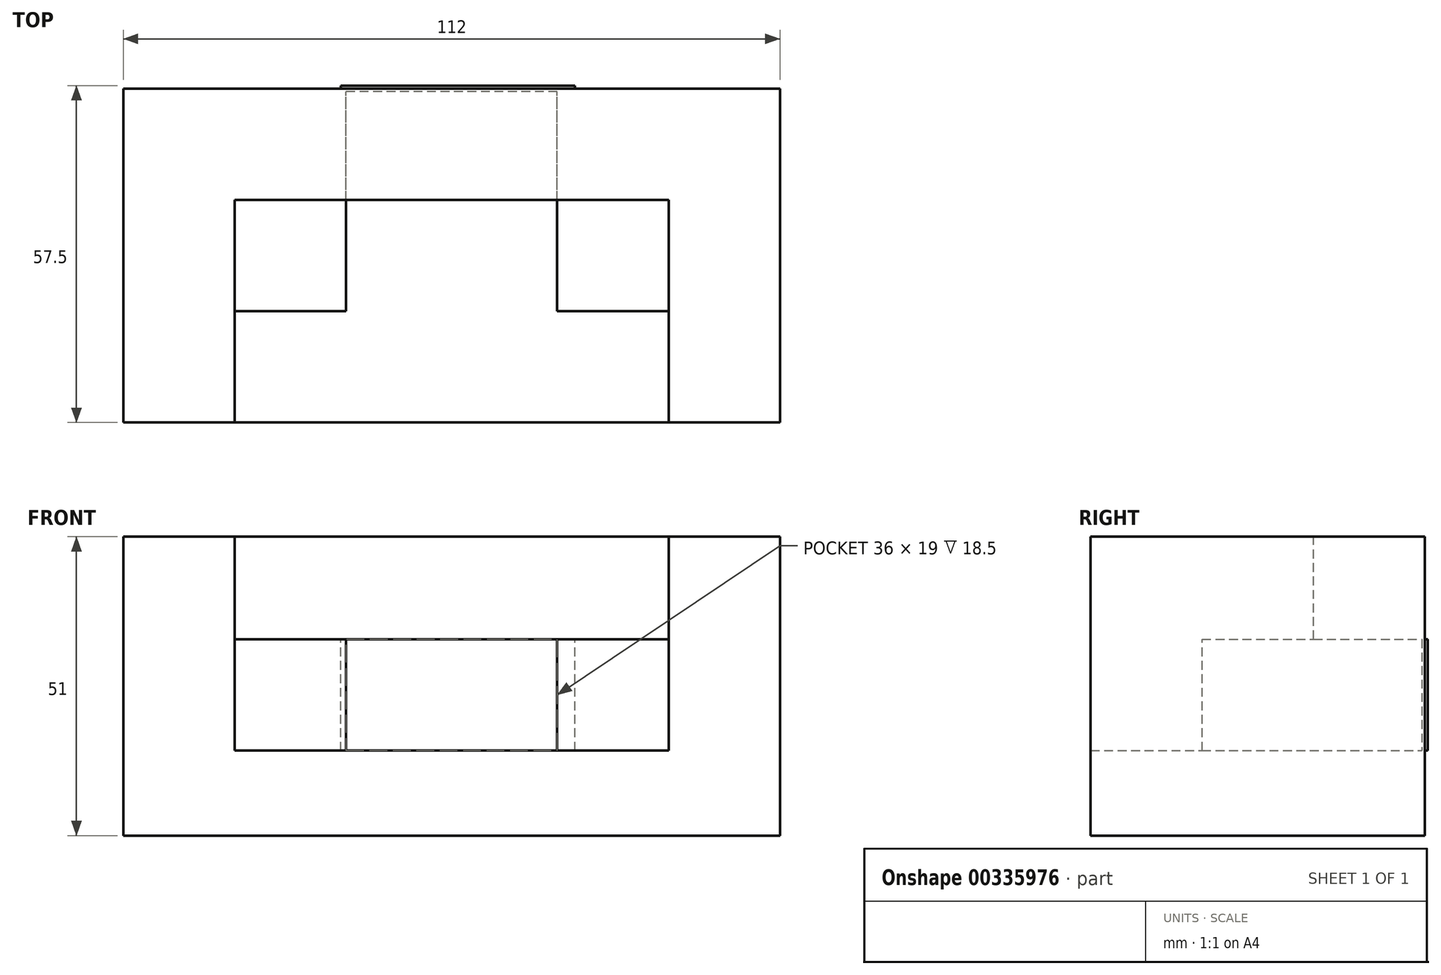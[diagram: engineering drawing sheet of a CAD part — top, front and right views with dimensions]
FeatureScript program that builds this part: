
annotation { "Feature Type Name" : "Feature", "Feature Type Description" : "" }
export const myFeature = defineFeature(function(context is Context, id is Id, definition is map)
    precondition{}
    {
        {
            var Q0;
            Q0=qCreatedBy(makeId("Front.planeOp"),FACE);
            var sketch = newSketch(context, id + "F0", { "sketchPlane" : qUnion([Q0])});
            skLineSegment(sketch, "E0", {"start": v(0, 0) * mm, "end": v(56, 0) * mm});
            skLineSegment(sketch, "E1", {"start": v(56, 0) * mm, "end": v(56, 51) * mm});
            skLineSegment(sketch, "E2", {"start": v(56, 51) * mm, "end": v(37, 51) * mm});
            skLineSegment(sketch, "E3", {"start": v(0, 0) * mm, "end": v(-56, 0) * mm});
            skLineSegment(sketch, "E4", {"start": v(-56, 0) * mm, "end": v(-56, 51) * mm});
            skLineSegment(sketch, "E5", {"start": v(-56, 51) * mm, "end": v(-37, 51) * mm});
            skLineSegment(sketch, "E6", {"start": v(-37, 51) * mm, "end": v(-37, 14.5) * mm});
            skLineSegment(sketch, "E7", {"start": v(-37, 14.5) * mm, "end": v(37, 14.5) * mm});
            skLineSegment(sketch, "E8", {"start": v(37, 14.5) * mm, "end": v(37, 51) * mm});
            skSolve(sketch);
        }
        {
            var Q0;
            Q0 = qSketchRegion(id + "F0", true);
            extrude(context, id + "F1", {"entities" : qUnion([Q0]), "depth" : 57 * mm});
        }
        {
            var Q0;
            Q0=makeQuery(id+"F1.opExtrude","CAP_FACE",FACE,{"disambiguationData":[OSD([sQuery(id+"F0.wireOp",EDGE,"E0"),sQuery(id+"F0.wireOp",EDGE,"E1"),sQuery(id+"F0.wireOp",EDGE,"E2"),sQuery(id+"F0.wireOp",EDGE,"E3"),sQuery(id+"F0.wireOp",EDGE,"E4"),sQuery(id+"F0.wireOp",EDGE,"E5"),sQuery(id+"F0.wireOp",EDGE,"E6"),sQuery(id+"F0.wireOp",EDGE,"E7"),sQuery(id+"F0.wireOp",EDGE,"E8")])],"isStart":true});
            var sketch = newSketch(context, id + "F2", { "sketchPlane" : qUnion([Q0])});
            skLineSegment(sketch, "E9.bottom", {"start": v(37, 14.5) * mm, "end": v(18, 14.5) * mm});
            skLineSegment(sketch, "E9.top", {"start": v(37, 33.5) * mm, "end": v(18, 33.5) * mm});
            skLineSegment(sketch, "E9.left", {"start": v(37, 14.5) * mm, "end": v(37, 33.5) * mm});
            skLineSegment(sketch, "E9.right", {"start": v(18, 14.5) * mm, "end": v(18, 33.5) * mm});
            skLineSegment(sketch, "E10.bottom", {"start": v(-37, 14.5) * mm, "end": v(-18, 14.5) * mm});
            skLineSegment(sketch, "E10.top", {"start": v(-37, 33.5) * mm, "end": v(-18, 33.5) * mm});
            skLineSegment(sketch, "E10.left", {"start": v(-37, 14.5) * mm, "end": v(-37, 33.5) * mm});
            skLineSegment(sketch, "E10.right", {"start": v(-18, 14.5) * mm, "end": v(-18, 33.5) * mm});
            skSolve(sketch);
        }
        {
            var Q0;
            Q0 = qSketchRegion(id + "F2", true);
            extrude(context, id + "F3", {"entities" : qUnion([Q0]), "operationType" : NewBodyOperationType.ADD, "oppositeDirection" : true, "depth" : 38 * mm});
        }
        {
            var Q0;
            Q0=makeQuery(id+"F3.boolean.opBoolean","MERGE",FACE,{"derivedFrom":[makeQuery(id+"F1.opExtrude","CAP_FACE",FACE,{"disambiguationData":[OSD([sQuery(id+"F0.wireOp",EDGE,"E0"),sQuery(id+"F0.wireOp",EDGE,"E1"),sQuery(id+"F0.wireOp",EDGE,"E2"),sQuery(id+"F0.wireOp",EDGE,"E3"),sQuery(id+"F0.wireOp",EDGE,"E4"),sQuery(id+"F0.wireOp",EDGE,"E5"),sQuery(id+"F0.wireOp",EDGE,"E6"),sQuery(id+"F0.wireOp",EDGE,"E7"),sQuery(id+"F0.wireOp",EDGE,"E8")])],"isStart":true}),makeQuery(id+"F3.opExtrude","CAP_FACE",FACE,{"disambiguationData":[OSD([sQuery(id+"F2.wireOp",EDGE,"E9.bottom"),sQuery(id+"F2.wireOp",EDGE,"E9.top"),sQuery(id+"F2.wireOp",EDGE,"E9.left"),sQuery(id+"F2.wireOp",EDGE,"E9.right")])],"isStart":true}),makeQuery(id+"F3.opExtrude","CAP_FACE",FACE,{"disambiguationData":[OSD([sQuery(id+"F2.wireOp",EDGE,"E10.bottom"),sQuery(id+"F2.wireOp",EDGE,"E10.top"),sQuery(id+"F2.wireOp",EDGE,"E10.left"),sQuery(id+"F2.wireOp",EDGE,"E10.right")])],"isStart":true})]});
            var sketch = newSketch(context, id + "F4", { "sketchPlane" : qUnion([Q0])});
            skLineSegment(sketch, "E11.bottom", {"start": v(-37, 33.5) * mm, "end": v(37, 33.5) * mm});
            skLineSegment(sketch, "E11.top", {"start": v(-37, 51) * mm, "end": v(37, 51) * mm});
            skLineSegment(sketch, "E11.left", {"start": v(-37, 33.5) * mm, "end": v(-37, 51) * mm});
            skLineSegment(sketch, "E11.right", {"start": v(37, 33.5) * mm, "end": v(37, 51) * mm});
            skSolve(sketch);
        }
        {
            var Q0;
            Q0 = qSketchRegion(id + "F4", true);
            extrude(context, id + "F5", {"entities" : qUnion([Q0]), "operationType" : NewBodyOperationType.ADD, "oppositeDirection" : true, "depth" : 19 * mm});
        }
        {
            var Q0;
            Q0=makeQuery(id+"F5.boolean.opBoolean","MERGE",FACE,{"derivedFrom":[makeQuery(id+"F3.boolean.opBoolean","MERGE",FACE,{"derivedFrom":[makeQuery(id+"F1.opExtrude","CAP_FACE",FACE,{"disambiguationData":[OSD([sQuery(id+"F0.wireOp",EDGE,"E0"),sQuery(id+"F0.wireOp",EDGE,"E1"),sQuery(id+"F0.wireOp",EDGE,"E2"),sQuery(id+"F0.wireOp",EDGE,"E3"),sQuery(id+"F0.wireOp",EDGE,"E4"),sQuery(id+"F0.wireOp",EDGE,"E5"),sQuery(id+"F0.wireOp",EDGE,"E6"),sQuery(id+"F0.wireOp",EDGE,"E7"),sQuery(id+"F0.wireOp",EDGE,"E8")])],"isStart":true}),makeQuery(id+"F3.opExtrude","CAP_FACE",FACE,{"disambiguationData":[OSD([sQuery(id+"F2.wireOp",EDGE,"E9.bottom"),sQuery(id+"F2.wireOp",EDGE,"E9.top"),sQuery(id+"F2.wireOp",EDGE,"E9.left"),sQuery(id+"F2.wireOp",EDGE,"E9.right")])],"isStart":true}),makeQuery(id+"F3.opExtrude","CAP_FACE",FACE,{"disambiguationData":[OSD([sQuery(id+"F2.wireOp",EDGE,"E10.bottom"),sQuery(id+"F2.wireOp",EDGE,"E10.top"),sQuery(id+"F2.wireOp",EDGE,"E10.left"),sQuery(id+"F2.wireOp",EDGE,"E10.right")])],"isStart":true})]}),makeQuery(id+"F5.opExtrude","CAP_FACE",FACE,{"disambiguationData":[OSD([sQuery(id+"F4.wireOp",EDGE,"E11.bottom"),sQuery(id+"F4.wireOp",EDGE,"E11.top"),sQuery(id+"F4.wireOp",EDGE,"E11.left"),sQuery(id+"F4.wireOp",EDGE,"E11.right")])],"isStart":true})]});
            var sketch = newSketch(context, id + "F6", { "sketchPlane" : qUnion([Q0])});
            skLineSegment(sketch, "E12.bottom", {"start": v(-21.05, 33.5) * mm, "end": v(18.95, 33.5) * mm});
            skLineSegment(sketch, "E12.top", {"start": v(-21.05, 14.5) * mm, "end": v(18.95, 14.5) * mm});
            skLineSegment(sketch, "E12.left", {"start": v(-21.05, 33.5) * mm, "end": v(-21.05, 14.5) * mm});
            skLineSegment(sketch, "E12.right", {"start": v(18.95, 33.5) * mm, "end": v(18.95, 14.5) * mm});
            skSolve(sketch);
        }
        {
            var Q0;
            Q0 = qSketchRegion(id + "F6", true);
            extrude(context, id + "F7", {"entities" : qUnion([Q0]), "operationType" : NewBodyOperationType.ADD, "endBound" : BoundingType.SYMMETRIC, "oppositeDirection" : true, "depth" : 1 * mm});
        }
    });
